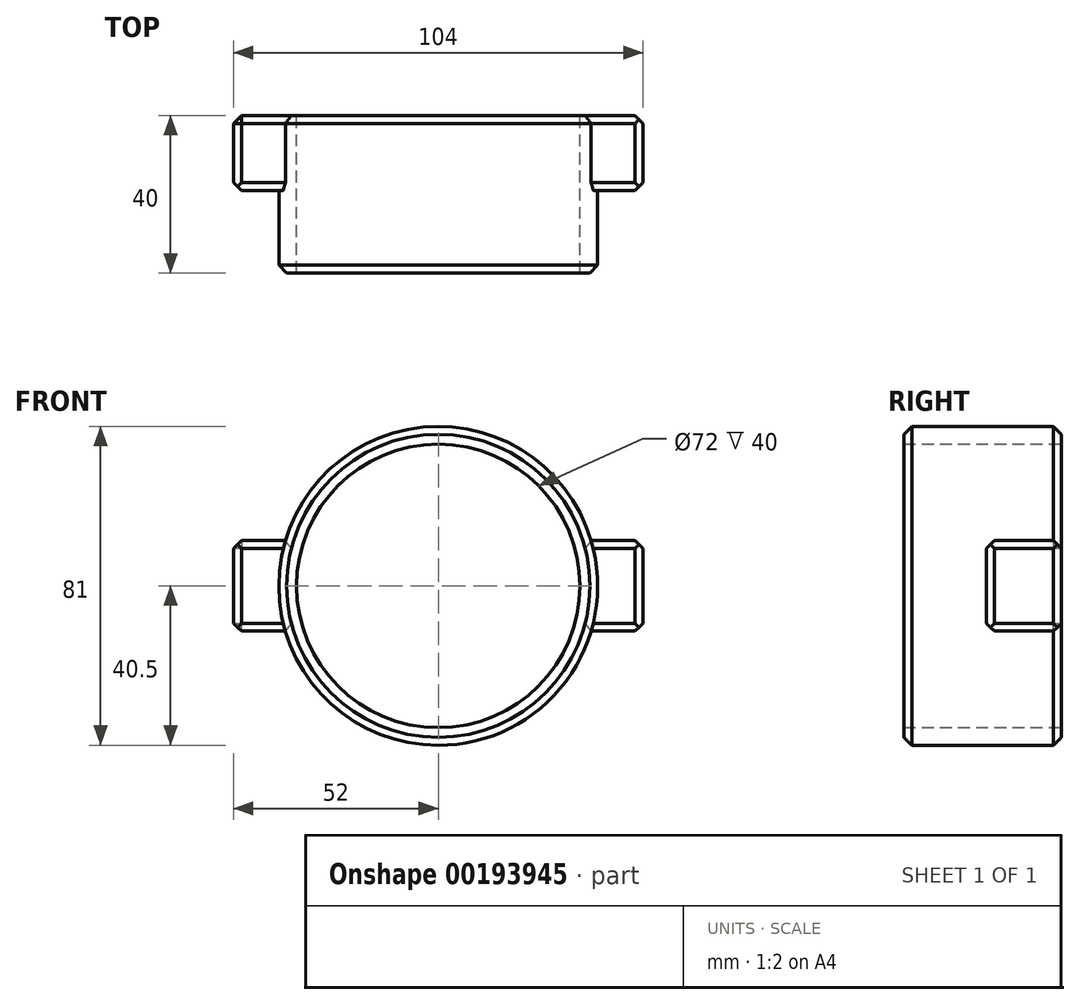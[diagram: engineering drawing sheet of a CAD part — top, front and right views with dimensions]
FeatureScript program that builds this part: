
annotation { "Feature Type Name" : "Feature", "Feature Type Description" : "" }
export const myFeature = defineFeature(function(context is Context, id is Id, definition is map)
    precondition{}
    {
        {
            var Q0;
            Q0=qCreatedBy(makeId("Front.planeOp"),FACE);
            var sketch = newSketch(context, id + "F0", { "sketchPlane" : qUnion([Q0])});
            skCircle(sketch, "E0", {"center": v(0, 0) * mm, "radius": 36 * mm});
            skCircle(sketch, "E1", {"center": v(0, 0) * mm, "radius": 40.5 * mm});
            skLineSegment(sketch, "E2.bottom", {"start": v(-52, -11.5) * mm, "end": v(52, -11.5) * mm});
            skLineSegment(sketch, "E2.top", {"start": v(-52, 11.5) * mm, "end": v(52, 11.5) * mm});
            skLineSegment(sketch, "E2.left", {"start": v(-52, -11.5) * mm, "end": v(-52, 11.5) * mm});
            skLineSegment(sketch, "E2.right", {"start": v(52, -11.5) * mm, "end": v(52, 11.5) * mm});
            skSolve(sketch);
        }
        {
            var Q0;
            {var subQ0=sQuery(id+"F0.wireOp",EDGE,"E2.bottom");var subQ1=sQuery(id+"F0.wireOp",EDGE,"E0");var subQ2=makeQuery(id+"F0.imprint","INTERSECT",VERTEX,{"disambiguationData":[OD(0.0)],"derivedFrom":[subQ1,subQ0]});Q0=makeQuery(id+"F0.imprint","IMPRINT",FACE,{"disambiguationData":[TD([[makeQuery(id+"F0.imprint","IMPRINT",EDGE,{"disambiguationData":[TD([[subQ2,-1.0]])],"derivedFrom":subQ1}),-1.0]])]});}
            var Q1;
            {var subQ0=sQuery(id+"F0.wireOp",EDGE,"E2.top");var subQ1=sQuery(id+"F0.wireOp",EDGE,"E0");var subQ2=makeQuery(id+"F0.imprint","INTERSECT",VERTEX,{"disambiguationData":[OD(0.0)],"derivedFrom":[subQ1,subQ0]});Q1=makeQuery(id+"F0.imprint","IMPRINT",FACE,{"disambiguationData":[TD([[makeQuery(id+"F0.imprint","IMPRINT",EDGE,{"disambiguationData":[TD([[subQ2,1.0]])],"derivedFrom":subQ1}),-1.0]])]});}
            var Q2;
            {var subQ0=sQuery(id+"F0.wireOp",EDGE,"E2.top");var subQ1=sQuery(id+"F0.wireOp",EDGE,"E0");var subQ2=makeQuery(id+"F0.imprint","INTERSECT",VERTEX,{"disambiguationData":[OD(0.0)],"derivedFrom":[subQ1,subQ0]});Q2=makeQuery(id+"F0.imprint","IMPRINT",FACE,{"disambiguationData":[TD([[makeQuery(id+"F0.imprint","IMPRINT",EDGE,{"disambiguationData":[TD([[subQ2,-1.0]])],"derivedFrom":subQ1}),-1.0]])]});}
            var Q3;
            {var subQ0=sQuery(id+"F0.wireOp",EDGE,"E2.top");var subQ1=sQuery(id+"F0.wireOp",EDGE,"E0");var subQ2=makeQuery(id+"F0.imprint","INTERSECT",VERTEX,{"disambiguationData":[OD(1.0)],"derivedFrom":[subQ1,subQ0]});Q3=makeQuery(id+"F0.imprint","IMPRINT",FACE,{"disambiguationData":[TD([[makeQuery(id+"F0.imprint","IMPRINT",EDGE,{"disambiguationData":[TD([[subQ2,1.0]])],"derivedFrom":subQ1}),-1.0]])]});}
            extrude(context, id + "F1", {"entities" : qUnion([Q0, Q1, Q2, Q3]), "depth" : 40 * mm});
        }
        {
            var Q0;
            Q0 = qSketchRegion(id + "F0", true);
            extrude(context, id + "F2", {"entities" : qUnion([Q0]), "operationType" : NewBodyOperationType.ADD, "depth" : 19 * mm});
        }
        {
            var Q0;
            Q0=makeQuery(id+"F2.opExtrude","SWEPT_EDGE",EDGE,{"disambiguationData":[OSD([sQuery(id+"F0.wireOp",EDGE,"E2.bottom"),sQuery(id+"F0.wireOp",EDGE,"E2.left")])]});
            var Q1;
            Q1=makeQuery(id+"F2.opExtrude","SWEPT_EDGE",EDGE,{"disambiguationData":[OSD([sQuery(id+"F0.wireOp",EDGE,"E2.top"),sQuery(id+"F0.wireOp",EDGE,"E2.left")])]});
            var Q2;
            Q2=makeQuery(id+"F2.opExtrude","SWEPT_EDGE",EDGE,{"disambiguationData":[OSD([sQuery(id+"F0.wireOp",EDGE,"E2.bottom"),sQuery(id+"F0.wireOp",EDGE,"E2.right")])]});
            var Q3;
            Q3=makeQuery(id+"F2.opExtrude","SWEPT_EDGE",EDGE,{"disambiguationData":[OSD([sQuery(id+"F0.wireOp",EDGE,"E2.top"),sQuery(id+"F0.wireOp",EDGE,"E2.right")])]});
            var Q4;
            Q4=makeQuery(id+"F1.opExtrude","CAP_EDGE",EDGE,{"disambiguationData":[OSD([sQuery(id+"F0.wireOp",EDGE,"E1")])],"isStart":false});
            var Q5;
            {var subQ0=sQuery(id+"F0.wireOp",EDGE,"E2.bottom");Q5=makeQuery(id+"F2.opExtrude","CAP_EDGE",EDGE,{"disambiguationData":[OSD([subQ0]),TDD([makeQuery(id+"F0.imprint","IMPRINT",EDGE,{"disambiguationData":[TD([[makeQuery(id+"F0.imprint","INTERSECT",VERTEX,{"derivedFrom":[subQ0,sQuery(id+"F0.wireOp",EDGE,"E2.right")]}),1.0]])],"derivedFrom":subQ0})])],"isStart":true});}
            var Q6;
            {var subQ1=sQuery(id+"F0.wireOp",EDGE,"E2.left");var subQ2=sQuery(id+"F0.wireOp",EDGE,"E2.bottom");var subQ3=sQuery(id+"F0.wireOp",EDGE,"E1");Q6=makeQuery(id+"F2.boolean.opBoolean","SPLIT",EDGE,{"disambiguationData":[TD([makeQuery(id+"F2.opExtrude","SWEPT_FACE",FACE,{"disambiguationData":[OSD([subQ2]),TDD([makeQuery(id+"F0.imprint","IMPRINT",EDGE,{"disambiguationData":[TD([[makeQuery(id+"F0.imprint","INTERSECT",VERTEX,{"derivedFrom":[subQ2,subQ1]}),-1.0]])],"derivedFrom":subQ2})])]})])],"derivedFrom":makeQuery(id+"F1.opExtrude","CAP_EDGE",EDGE,{"disambiguationData":[OSD([subQ3])],"isStart":true})});}
            var Q7;
            {var subQ0=sQuery(id+"F0.wireOp",EDGE,"E2.bottom");Q7=makeQuery(id+"F2.opExtrude","CAP_EDGE",EDGE,{"disambiguationData":[OSD([subQ0]),TDD([makeQuery(id+"F0.imprint","IMPRINT",EDGE,{"disambiguationData":[TD([[makeQuery(id+"F0.imprint","INTERSECT",VERTEX,{"derivedFrom":[subQ0,sQuery(id+"F0.wireOp",EDGE,"E2.left")]}),-1.0]])],"derivedFrom":subQ0})])],"isStart":true});}
            var Q8;
            Q8=makeQuery(id+"F2.opExtrude","CAP_EDGE",EDGE,{"disambiguationData":[OSD([sQuery(id+"F0.wireOp",EDGE,"E2.left")])],"isStart":true});
            var Q9;
            {var subQ0=sQuery(id+"F0.wireOp",EDGE,"E2.top");Q9=makeQuery(id+"F2.opExtrude","CAP_EDGE",EDGE,{"disambiguationData":[OSD([subQ0]),TDD([makeQuery(id+"F0.imprint","IMPRINT",EDGE,{"disambiguationData":[TD([[makeQuery(id+"F0.imprint","INTERSECT",VERTEX,{"derivedFrom":[subQ0,sQuery(id+"F0.wireOp",EDGE,"E2.left")]}),-1.0]])],"derivedFrom":subQ0})])],"isStart":true});}
            var Q10;
            {var subQ1=sQuery(id+"F0.wireOp",EDGE,"E2.left");var subQ2=sQuery(id+"F0.wireOp",EDGE,"E2.top");var subQ3=sQuery(id+"F0.wireOp",EDGE,"E1");Q10=makeQuery(id+"F2.boolean.opBoolean","SPLIT",EDGE,{"disambiguationData":[TD([makeQuery(id+"F2.opExtrude","SWEPT_FACE",FACE,{"disambiguationData":[OSD([subQ2]),TDD([makeQuery(id+"F0.imprint","IMPRINT",EDGE,{"disambiguationData":[TD([[makeQuery(id+"F0.imprint","INTERSECT",VERTEX,{"derivedFrom":[subQ2,subQ1]}),-1.0]])],"derivedFrom":subQ2})])]})])],"derivedFrom":makeQuery(id+"F1.opExtrude","CAP_EDGE",EDGE,{"disambiguationData":[OSD([subQ3])],"isStart":true})});}
            var Q11;
            Q11=makeQuery(id+"F2.opExtrude","CAP_EDGE",EDGE,{"disambiguationData":[OSD([sQuery(id+"F0.wireOp",EDGE,"E2.right")])],"isStart":false});
            var Q12;
            Q12=makeQuery(id+"F2.opExtrude","CAP_EDGE",EDGE,{"disambiguationData":[OSD([sQuery(id+"F0.wireOp",EDGE,"E2.left")])],"isStart":false});
            chamfer(context, id + "F3", {"entities" : qUnion([Q0, Q1, Q2, Q3, Q4, Q5, Q6, Q7, Q8, Q9, Q10, Q11, Q12]), "width" : 2 * mm, "tangentPropagation" : true});
        }
        {
            var Q0;
            Q0=makeQuery(id+"F2.opExtrude","CAP_EDGE",EDGE,{"disambiguationData":[OSD([sQuery(id+"F0.wireOp",EDGE,"E2.right")])],"isStart":true});
            chamfer(context, id + "F4", {"entities" : qUnion([Q0]), "width" : 2 * mm, "tangentPropagation" : true});
        }
        {
            var Q0;
            {var subQ0=sQuery(id+"F0.wireOp",EDGE,"E2.top");Q0=makeQuery(id+"F2.opExtrude","CAP_EDGE",EDGE,{"disambiguationData":[OSD([subQ0]),TDD([makeQuery(id+"F0.imprint","IMPRINT",EDGE,{"disambiguationData":[TD([[makeQuery(id+"F0.imprint","INTERSECT",VERTEX,{"derivedFrom":[subQ0,sQuery(id+"F0.wireOp",EDGE,"E2.right")]}),1.0]])],"derivedFrom":subQ0})])],"isStart":false});}
            var Q1;
            {var subQ0=sQuery(id+"F0.wireOp",EDGE,"E2.top");Q1=makeQuery(id+"F2.opExtrude","CAP_EDGE",EDGE,{"disambiguationData":[OSD([subQ0]),TDD([makeQuery(id+"F0.imprint","IMPRINT",EDGE,{"disambiguationData":[TD([[makeQuery(id+"F0.imprint","INTERSECT",VERTEX,{"derivedFrom":[subQ0,sQuery(id+"F0.wireOp",EDGE,"E2.right")]}),1.0]])],"derivedFrom":subQ0})])],"isStart":true});}
            var Q2;
            {var subQ0=sQuery(id+"F0.wireOp",EDGE,"E2.top");Q2=makeQuery(id+"F2.opExtrude","CAP_EDGE",EDGE,{"disambiguationData":[OSD([subQ0]),TDD([makeQuery(id+"F0.imprint","IMPRINT",EDGE,{"disambiguationData":[TD([[makeQuery(id+"F0.imprint","INTERSECT",VERTEX,{"derivedFrom":[subQ0,sQuery(id+"F0.wireOp",EDGE,"E2.left")]}),-1.0]])],"derivedFrom":subQ0})])],"isStart":false});}
            var Q3;
            {var subQ0=sQuery(id+"F0.wireOp",EDGE,"E2.bottom");Q3=makeQuery(id+"F2.opExtrude","CAP_EDGE",EDGE,{"disambiguationData":[OSD([subQ0]),TDD([makeQuery(id+"F0.imprint","IMPRINT",EDGE,{"disambiguationData":[TD([[makeQuery(id+"F0.imprint","INTERSECT",VERTEX,{"derivedFrom":[subQ0,sQuery(id+"F0.wireOp",EDGE,"E2.left")]}),-1.0]])],"derivedFrom":subQ0})])],"isStart":false});}
            var Q4;
            {var subQ0=sQuery(id+"F0.wireOp",EDGE,"E2.bottom");Q4=makeQuery(id+"F2.opExtrude","CAP_EDGE",EDGE,{"disambiguationData":[OSD([subQ0]),TDD([makeQuery(id+"F0.imprint","IMPRINT",EDGE,{"disambiguationData":[TD([[makeQuery(id+"F0.imprint","INTERSECT",VERTEX,{"derivedFrom":[subQ0,sQuery(id+"F0.wireOp",EDGE,"E2.right")]}),1.0]])],"derivedFrom":subQ0})])],"isStart":false});}
            chamfer(context, id + "F5", {"entities" : qUnion([Q0, Q1, Q2, Q3, Q4]), "width" : 2 * mm, "tangentPropagation" : true});
        }
    });
